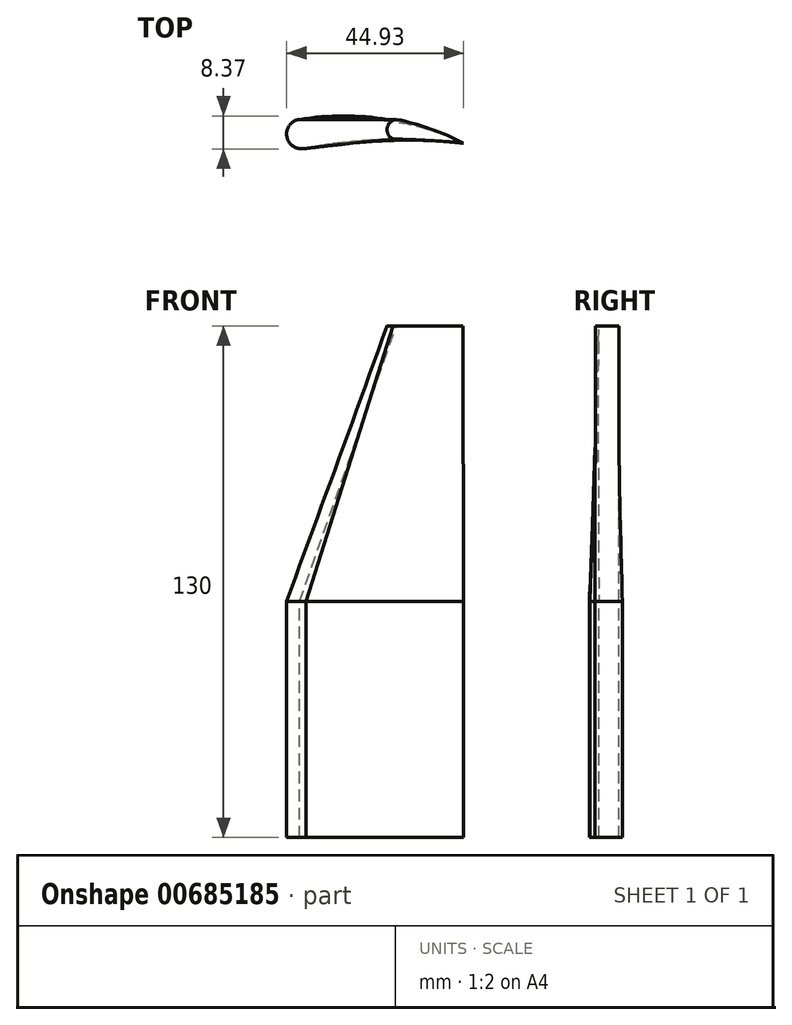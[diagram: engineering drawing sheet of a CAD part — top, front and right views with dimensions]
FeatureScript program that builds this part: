
annotation { "Feature Type Name" : "Feature", "Feature Type Description" : "" }
export const myFeature = defineFeature(function(context is Context, id is Id, definition is map)
    precondition{}
    {
        {
            var Q0;
            Q0=qCreatedBy(makeId("Top.planeOp"),FACE);
            var sketch = newSketch(context, id + "F0", { "sketchPlane" : qUnion([Q0])});
            skArc(sketch, "E0", {"start": v(41.6, -6.07) * mm, "mid": v(21.27, 0.15) * mm, "end": v(0, 0) * mm});
            skArc(sketch, "E1", {"start": v(0, 0) * mm, "mid": v(-3.24, -4.5) * mm, "end": v(1.55, -7.3) * mm});
            skArc(sketch, "E2", {"start": v(41.6, -6.07) * mm, "mid": v(21.53, -5.15) * mm, "end": v(1.55, -7.3) * mm});
            skSolve(sketch);
        }
        {
            var Q0;
            Q0=makeQuery(id+"F0.imprint","IMPRINT",FACE,{"disambiguationData":[TD([[makeQuery(id+"F0.imprint","IMPRINT",EDGE,{"derivedFrom":sQuery(id+"F0.wireOp",EDGE,"E0")}),1.0]])]});
            cPlane(context, id + "F1", {"entities" : qUnion([Q0]), "cplaneType" : CPlaneType.OFFSET, "offset" : 60 * mm, "width" : 150 * mm, "height" : 150 * mm});
        }
        {
            var Q0;
            Q0=qCreatedBy(id+"F1.planeOp",FACE);
            var sketch = newSketch(context, id + "F2", { "sketchPlane" : qUnion([Q0])});
            skArc(sketch, "E3.0", {"start": v(0, 0) * mm, "mid": v(-3.24, -4.5) * mm, "end": v(1.55, -7.3) * mm});
            skArc(sketch, "E3.1", {"start": v(41.6, -6.07) * mm, "mid": v(21.53, -5.15) * mm, "end": v(1.55, -7.3) * mm});
            skArc(sketch, "E3.2", {"start": v(41.6, -6.07) * mm, "mid": v(21.27, 0.15) * mm, "end": v(0, 0) * mm});
            skSolve(sketch);
        }
        {
            var Q0;
            Q0=qCreatedBy(id+"F1.planeOp",FACE);
            cPlane(context, id + "F3", {"entities" : qUnion([Q0]), "cplaneType" : CPlaneType.OFFSET, "offset" : 70 * mm, "width" : 150 * mm, "height" : 150 * mm});
        }
        {
            var Q0;
            Q0=makeQuery(id+"F0.imprint","IMPRINT",FACE,{"disambiguationData":[TD([[makeQuery(id+"F0.imprint","IMPRINT",EDGE,{"derivedFrom":sQuery(id+"F0.wireOp",EDGE,"E0")}),1.0]])]});
            var Q1;
            Q1=makeQuery(id+"F2.imprint","IMPRINT",FACE,{"disambiguationData":[TD([[makeQuery(id+"F2.imprint","IMPRINT",EDGE,{"derivedFrom":sQuery(id+"F2.wireOp",EDGE,"E3.0")}),1.0]])]});
            loft(context, id + "F4", {"sheetProfilesArray" : [{ "sheetProfileEntities" : qUnion([Q0]) }, { "sheetProfileEntities" : qUnion([Q1]) }]});
        }
        {
            var Q0;
            Q0=qCreatedBy(id+"F3.planeOp",FACE);
            var sketch = newSketch(context, id + "F5", { "sketchPlane" : qUnion([Q0])});
            skArc(sketch, "E4", {"start": v(41.52, -5.98) * mm, "mid": v(33.27, -2.41) * mm, "end": v(24.6, 0) * mm});
            skArc(sketch, "E5", {"start": v(24.6, 0) * mm, "mid": v(22.22, -2.16) * mm, "end": v(23.73, -5) * mm});
            skArc(sketch, "E6", {"start": v(41.52, -5.98) * mm, "mid": v(32.63, -5.35) * mm, "end": v(23.73, -5) * mm});
            skSolve(sketch);
        }
        {
            var Q0;
            Q0=makeQuery(id+"F4.opLoft","CAP_FACE",FACE,{"disambiguationData":[OSD([makeQuery(id+"F2.imprint","IMPRINT",FACE,{"disambiguationData":[TD([[makeQuery(id+"F2.imprint","IMPRINT",EDGE,{"derivedFrom":sQuery(id+"F2.wireOp",EDGE,"E3.0")}),1.0]])]})])],"isStart":true});
            var Q1;
            Q1=makeQuery(id+"F5.imprint","IMPRINT",FACE,{"disambiguationData":[TD([[makeQuery(id+"F5.imprint","IMPRINT",EDGE,{"derivedFrom":sQuery(id+"F5.wireOp",EDGE,"E4")}),1.0]])]});
            loft(context, id + "F6", {"sheetProfilesArray" : [{ "sheetProfileEntities" : qUnion([Q0]) }, { "sheetProfileEntities" : qUnion([Q1]) }]});
        }
    });
